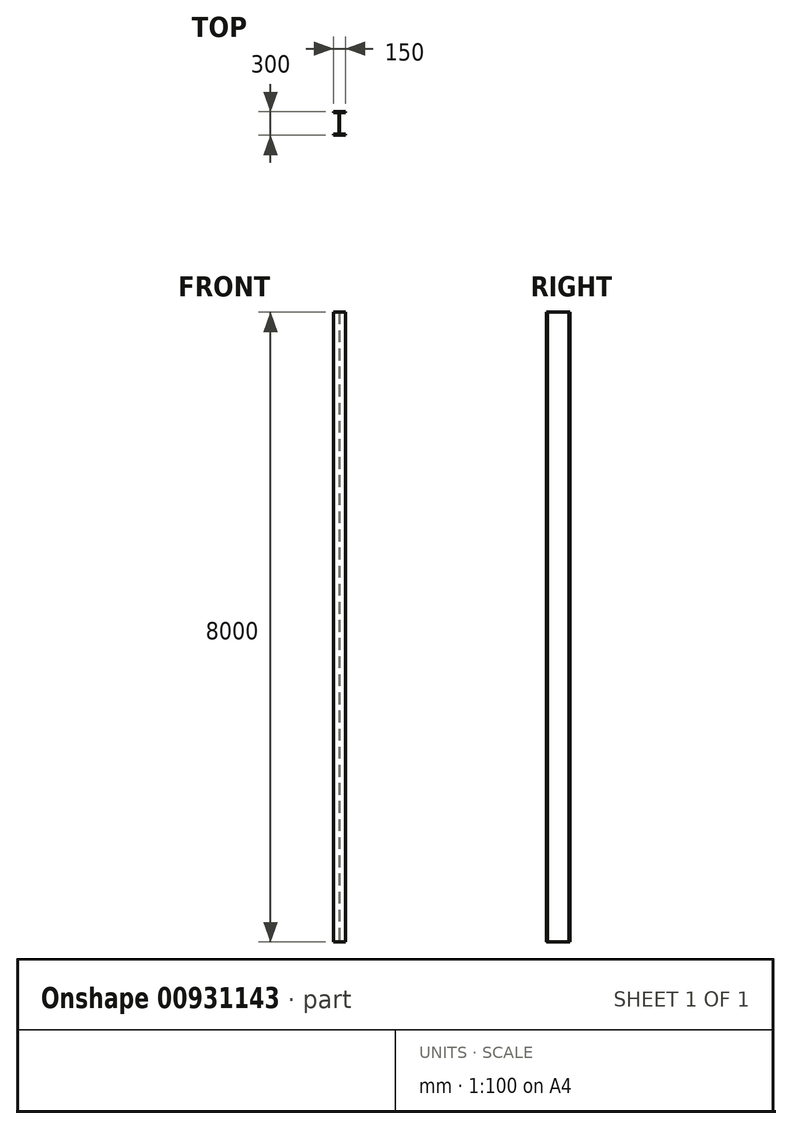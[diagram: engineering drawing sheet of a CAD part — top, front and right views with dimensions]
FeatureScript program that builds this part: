
annotation { "Feature Type Name" : "Feature", "Feature Type Description" : "" }
export const myFeature = defineFeature(function(context is Context, id is Id, definition is map)
    precondition{}
    {
        {
            var Q0;
            Q0=qCreatedBy(makeId("Top.planeOp"),FACE);
            var sketch = newSketch(context, id + "F0", { "sketchPlane" : qUnion([Q0])});
            skPoint(sketch, "E0", {"position": v(3.5, 0) * mm});
            skLineSegment(sketch, "E1", {"start": v(3.5, 0) * mm, "end": v(3.5, 124.3) * mm});
            skLineSegment(sketch, "E2", {"start": v(18.5, 139.3) * mm, "end": v(75.1, 139.3) * mm});
            skLineSegment(sketch, "E3", {"start": v(75.1, 139.3) * mm, "end": v(75.1, 150) * mm});
            skLineSegment(sketch, "E4", {"start": v(75.1, 150) * mm, "end": v(-74.9, 150) * mm});
            skLineSegment(sketch, "E5", {"start": v(-74.9, 150) * mm, "end": v(-74.9, 139.3) * mm});
            skLineSegment(sketch, "E6", {"start": v(-74.9, 139.3) * mm, "end": v(-18.3, 139.3) * mm});
            skLineSegment(sketch, "E7", {"start": v(-3.3, 124.3) * mm, "end": v(-3.3, 0) * mm});
            skPoint(sketch, "E8", {"position": v(-3.3, 0) * mm});
            skLineSegment(sketch, "E9", {"start": v(-3.3, 0) * mm, "end": v(-3.3, -124.3) * mm});
            skLineSegment(sketch, "E10", {"start": v(-18.3, -139.3) * mm, "end": v(-74.9, -139.3) * mm});
            skLineSegment(sketch, "E11", {"start": v(-74.9, -139.3) * mm, "end": v(-74.9, -150) * mm});
            skLineSegment(sketch, "E12", {"start": v(-74.9, -150) * mm, "end": v(75.1, -150) * mm});
            skLineSegment(sketch, "E13", {"start": v(75.1, -150) * mm, "end": v(75.1, -139.3) * mm});
            skLineSegment(sketch, "E14", {"start": v(75.1, -139.3) * mm, "end": v(18.5, -139.3) * mm});
            skLineSegment(sketch, "E15", {"start": v(3.5, -124.3) * mm, "end": v(3.5, 0) * mm});
            skPoint(sketch, "E16.visualSharp", {"position": v(3.5, 139.3) * mm});
            skArc(sketch, "E16.filletArc", {"start": v(18.5, 139.3) * mm, "mid": v(7.9, 134.9) * mm, "end": v(3.5, 124.3) * mm});
            skPoint(sketch, "E17.visualSharp", {"position": v(-3.3, 139.3) * mm});
            skArc(sketch, "E17.filletArc", {"start": v(-3.3, 124.3) * mm, "mid": v(-7.7, 134.9) * mm, "end": v(-18.3, 139.3) * mm});
            skPoint(sketch, "E18.visualSharp", {"position": v(3.5, -139.3) * mm});
            skArc(sketch, "E18.filletArc", {"start": v(3.5, -124.3) * mm, "mid": v(7.9, -134.9) * mm, "end": v(18.5, -139.3) * mm});
            skPoint(sketch, "E19.visualSharp", {"position": v(-3.3, -139.3) * mm});
            skArc(sketch, "E19.filletArc", {"start": v(-18.3, -139.3) * mm, "mid": v(-7.7, -134.9) * mm, "end": v(-3.3, -124.3) * mm});
            skSolve(sketch);
        }
        {
            var Q0;
            Q0=makeQuery(id+"F0.imprint","IMPRINT",FACE,{"disambiguationData":[TD([[makeQuery(id+"F0.imprint","IMPRINT",EDGE,{"derivedFrom":sQuery(id+"F0.wireOp",EDGE,"E1")}),1.0]])]});
            extrude(context, id + "F1", {"entities" : qUnion([Q0]), "depth" : 8000 * mm, "offsetDistance" : 25 * mm});
        }
    });
